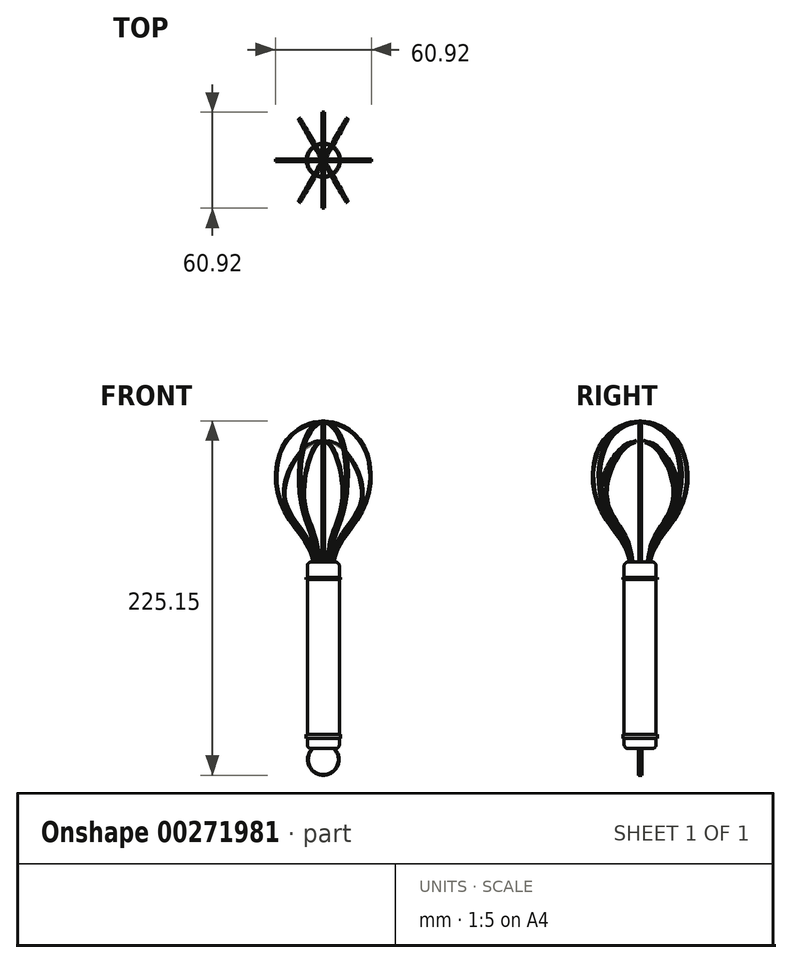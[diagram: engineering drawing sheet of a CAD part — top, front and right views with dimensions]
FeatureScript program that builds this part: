
annotation { "Feature Type Name" : "Feature", "Feature Type Description" : "" }
export const myFeature = defineFeature(function(context is Context, id is Id, definition is map)
    precondition{}
    {
        {
            var Q0;
            Q0=qCreatedBy(makeId("Front.planeOp"),FACE);
            var sketch = newSketch(context, id + "F0", { "sketchPlane" : qUnion([Q0])});
            skLineSegment(sketch, "E0", {"start": v(0, 93.33) * mm, "end": v(0, -97.58) * mm, "construction": true});
            skLineSegment(sketch, "E1.bottom", {"start": v(0, -73.35) * mm, "end": v(-7.62, -73.35) * mm});
            skLineSegment(sketch, "E1.top", {"start": v(0, 45.21) * mm, "end": v(-7.62, 45.21) * mm});
            skLineSegment(sketch, "E1.left", {"start": v(0, -73.35) * mm, "end": v(0, 45.21) * mm});
            skLineSegment(sketch, "E1.right", {"start": v(-10.16, -70.8) * mm, "end": v(-10.16, 42.67) * mm});
            skPoint(sketch, "E2.visualSharp", {"position": v(-10.16, -73.35) * mm});
            skArc(sketch, "E2.filletArc", {"start": v(-10.16, -70.8) * mm, "mid": v(-9.42, -72.6) * mm, "end": v(-7.62, -73.35) * mm});
            skPoint(sketch, "E3.visualSharp", {"position": v(-10.16, 45.21) * mm});
            skArc(sketch, "E3.filletArc", {"start": v(-7.62, 45.21) * mm, "mid": v(-9.42, 44.47) * mm, "end": v(-10.16, 42.67) * mm});
            skArc(sketch, "E4", {"start": v(-7.18, -73.35) * mm, "mid": v(0, -90.25) * mm, "end": v(7.18, -73.35) * mm});
            skPoint(sketch, "E5", {"position": v(-7.18, -73.35) * mm});
            skPoint(sketch, "E6", {"position": v(7.18, -73.35) * mm});
            skArc(sketch, "E7.0", {"start": v(-6.88, -73.63) * mm, "mid": v(0, -89.84) * mm, "end": v(6.88, -73.63) * mm});
            skFitSpline(sketch, "E8", {"points": [v(-6.88, -73.63) * mm, v(-6.6, -73.35) * mm], "startDerivative": vector(0.28, 0.28) * mm, "endDerivative": vector(0.28, 0.28) * mm});
            skLineSegment(sketch, "E9", {"start": v(-6.6, -73.35) * mm, "end": v(7.18, -73.35) * mm});
            skFitSpline(sketch, "E10", {"points": [v(6.88, -73.63) * mm, v(6.61, -73.35) * mm], "startDerivative": vector(-0.27, 0.28) * mm, "endDerivative": vector(-0.27, 0.28) * mm});
            skFitSpline(sketch, "E11", {"points": [v(-6.56, 45.21) * mm, v(-11.07, 60.4) * mm, v(-25.22, 86.5) * mm, v(-12.08, 117.9) * mm, v(0, 122.64) * mm], "startDerivative": vector(-9.97, 69.88) * mm, "endDerivative": vector(61.82, 8.5) * mm});
            skFitSpline(sketch, "E12.0", {"points": [v(-5.56, 45.35) * mm, v(-5.77, 46.81) * mm, v(-6.08, 49.02) * mm, v(-6.7, 52.03) * mm, v(-7.3, 54.33) * mm, v(-8.11, 56.67) * mm, v(-8.99, 58.67) * mm, v(-9.83, 60.3) * mm, v(-10.78, 61.93) * mm, v(-12.15, 64) * mm, v(-13.97, 66.51) * mm, v(-16.52, 69.96) * mm, v(-19.08, 73.57) * mm, v(-21.28, 77.37) * mm, v(-22.66, 80.33) * mm, v(-23.52, 82.89) * mm, v(-24, 85) * mm, v(-24.24, 86.62) * mm, v(-24.35, 88.29) * mm, v(-24.33, 90.56) * mm, v(-24.02, 93.48) * mm, v(-23.25, 97.04) * mm, v(-21.74, 101.76) * mm, v(-19.63, 106.3) * mm, v(-17.17, 110.37) * mm, v(-15.2, 113.12) * mm, v(-13.52, 115.1) * mm, v(-12.18, 116.45) * mm, v(-10.86, 117.64) * mm, v(-9.26, 118.81) * mm, v(-6.75, 120.17) * mm, v(-3.67, 121.1) * mm, v(-1.15, 121.46) * mm, v(0.14, 121.64) * mm]});
            skLineSegment(sketch, "E13", {"start": v(-5.56, 45.35) * mm, "end": v(-5.56, 45.21) * mm});
            skLineSegment(sketch, "E14", {"start": v(0.14, 121.64) * mm, "end": v(0, 122.64) * mm});
            skFitSpline(sketch, "E15.MirrorCS", {"points": [v(6.56, 45.21) * mm, v(11.07, 60.4) * mm, v(25.22, 86.5) * mm, v(12.08, 117.9) * mm, v(0, 122.64) * mm], "startDerivative": vector(9.97, 69.88) * mm, "endDerivative": vector(-61.82, 8.5) * mm});
            skFitSpline(sketch, "E16.0", {"points": [v(5.56, 45.35) * mm, v(5.77, 46.81) * mm, v(6.08, 49.02) * mm, v(6.7, 52.03) * mm, v(7.3, 54.33) * mm, v(8.11, 56.67) * mm, v(8.99, 58.67) * mm, v(9.83, 60.3) * mm, v(10.78, 61.93) * mm, v(12.15, 64) * mm, v(13.97, 66.51) * mm, v(16.52, 69.96) * mm, v(19.08, 73.57) * mm, v(21.28, 77.37) * mm, v(22.66, 80.33) * mm, v(23.52, 82.89) * mm, v(24, 85) * mm, v(24.24, 86.62) * mm, v(24.35, 88.29) * mm, v(24.33, 90.56) * mm, v(24.02, 93.48) * mm, v(23.25, 97.04) * mm, v(21.74, 101.76) * mm, v(19.63, 106.3) * mm, v(17.17, 110.37) * mm, v(15.2, 113.12) * mm, v(13.52, 115.1) * mm, v(12.18, 116.45) * mm, v(10.86, 117.64) * mm, v(9.26, 118.81) * mm, v(6.75, 120.17) * mm, v(3.67, 121.1) * mm, v(1.15, 121.46) * mm, v(-0.14, 121.64) * mm]});
            skLineSegment(sketch, "E17", {"start": v(0, 45.21) * mm, "end": v(6.56, 45.21) * mm});
            skLineSegment(sketch, "E18", {"start": v(5.56, 45.35) * mm, "end": v(5.56, 45.21) * mm});
            skLineSegment(sketch, "E19.bottom", {"start": v(-10.16, 34.07) * mm, "end": v(0, 34.07) * mm});
            skLineSegment(sketch, "E19.top", {"start": v(-10.16, 35.42) * mm, "end": v(0, 35.42) * mm});
            skLineSegment(sketch, "E19.left", {"start": v(-10.16, 34.07) * mm, "end": v(-10.16, 35.42) * mm});
            skLineSegment(sketch, "E19.right", {"start": v(0, 34.07) * mm, "end": v(0, 35.42) * mm});
            skLineSegment(sketch, "E20.bottom", {"start": v(0, -66.97) * mm, "end": v(-10.16, -66.97) * mm});
            skLineSegment(sketch, "E20.top", {"start": v(0, -64.16) * mm, "end": v(-10.16, -64.16) * mm});
            skLineSegment(sketch, "E20.left", {"start": v(0, -66.97) * mm, "end": v(0, -64.16) * mm});
            skLineSegment(sketch, "E20.right", {"start": v(-10.16, -66.97) * mm, "end": v(-10.16, -64.16) * mm});
            skLineSegment(sketch, "E21.bottom", {"start": v(-10.16, 35.42) * mm, "end": v(-10.84, 35.42) * mm});
            skLineSegment(sketch, "E21.top", {"start": v(-10.16, 34.07) * mm, "end": v(-10.84, 34.07) * mm});
            skLineSegment(sketch, "E21.left", {"start": v(-10.16, 35.42) * mm, "end": v(-10.16, 34.07) * mm});
            skLineSegment(sketch, "E21.right", {"start": v(-10.84, 35.42) * mm, "end": v(-10.84, 34.07) * mm});
            skLineSegment(sketch, "E22.bottom", {"start": v(-10.16, -66.97) * mm, "end": v(-10.84, -66.97) * mm});
            skLineSegment(sketch, "E22.top", {"start": v(-10.16, -64.16) * mm, "end": v(-10.84, -64.16) * mm});
            skLineSegment(sketch, "E22.right", {"start": v(-10.84, -66.97) * mm, "end": v(-10.84, -64.16) * mm});
            skSolve(sketch);
        }
        {
            var Q0;
            Q0=makeQuery(id+"F0.imprint","IMPRINT",FACE,{"disambiguationData":[TD([[makeQuery(id+"F0.imprint","IMPRINT",EDGE,{"derivedFrom":sQuery(id+"F0.wireOp",EDGE,"E1.top")}),1.0]])]});
            var Q1;
            Q1=sQuery(id+"F0.wireOp",EDGE,"E1.left");
            revolve(context, id + "F1", {"entities" : qUnion([Q0]), "axis" : qUnion([Q1]), "revolveType" : RevolveType.FULL});
        }
        {
            var Q0;
            {var subQ1=sQuery(id+"F0.wireOp",EDGE,"E4");Q0=makeQuery(id+"F0.imprint","IMPRINT",FACE,{"disambiguationData":[TD([[makeQuery(id+"F0.imprint","IMPRINT",EDGE,{"derivedFrom":subQ1}),1.0]])]});}
            extrude(context, id + "F2", {"entities" : qUnion([Q0]), "operationType" : NewBodyOperationType.ADD, "endBound" : BoundingType.SYMMETRIC, "depth" : 2.3 * mm});
        }
        {
            var Q0;
            Q0=makeQuery(id+"F2.opExtrude","CAP_EDGE",EDGE,{"disambiguationData":[OSD([sQuery(id+"F0.wireOp",EDGE,"E7.0")])],"isStart":false});
            fillet(context, id + "F3", {"entities" : qUnion([Q0]), "radius" : 0.43 * mm, "tangentPropagation" : true, "allowEdgeOverflow" : false});
        }
        {
            var Q0;
            Q0=makeQuery(id+"F2.opExtrude","CAP_EDGE",EDGE,{"disambiguationData":[OSD([sQuery(id+"F0.wireOp",EDGE,"E7.0")])],"isStart":true});
            fillet(context, id + "F4", {"entities" : qUnion([Q0]), "radius" : 0.67 * mm, "tangentPropagation" : true, "allowEdgeOverflow" : false});
        }
        {
            var Q0;
            Q0=makeQuery(id+"F3.opFillet","BLEND_EDGE",EDGE,{"blendedFrom":[makeQuery(id+"F2.opExtrude","CAP_EDGE",EDGE,{"disambiguationData":[OSD([sQuery(id+"F0.wireOp",EDGE,"E7.0")])],"isStart":false}),makeQuery(id+"F2.opExtrude","SWEPT_FACE",FACE,{"disambiguationData":[OSD([sQuery(id+"F0.wireOp",EDGE,"E4")])]})],"blendedInto":[makeQuery(id+"F2.opExtrude","SWEPT_FACE",FACE,{"disambiguationData":[OSD([sQuery(id+"F0.wireOp",EDGE,"E4")])]})]});
            fillet(context, id + "F5", {"entities" : qUnion([Q0]), "radius" : 0.17 * mm, "tangentPropagation" : true, "allowEdgeOverflow" : false});
        }
        {
            var Q0;
            {var subQ4=sQuery(id+"F0.wireOp",EDGE,"E11");Q0=makeQuery(id+"F0.imprint","IMPRINT",FACE,{"disambiguationData":[TD([[makeQuery(id+"F0.imprint","IMPRINT",EDGE,{"derivedFrom":subQ4}),-1.0]])]});}
            var Q1;
            {var subQ5=sQuery(id+"F0.wireOp",EDGE,"E14");Q1=makeQuery(id+"F0.imprint","IMPRINT",FACE,{"disambiguationData":[TD([[makeQuery(id+"F0.imprint","IMPRINT",EDGE,{"derivedFrom":subQ5}),-1.0]])]});}
            extrude(context, id + "F6", {"entities" : qUnion([Q0, Q1]), "endBound" : BoundingType.SYMMETRIC, "oppositeDirection" : true, "depth" : 0.5 * mm, "hasDraft" : true, "draftAngle" : 3 * degree});
        }
        {
            var Q0;
            Q0=qCreatedBy(makeId("Right.planeOp"),FACE);
            var sketch = newSketch(context, id + "F7", { "sketchPlane" : qUnion([Q0])});
            skFitSpline(sketch, "E23", {"points": [v(-6.67, 45.23) * mm, v(-10.44, 55.68) * mm, v(-27.99, 84.43) * mm, v(-25.65, 119.53) * mm, v(-10.27, 132.73) * mm, v(0, 134.9) * mm], "startDerivative": vector(-14.2, 65.3) * mm, "endDerivative": vector(68.76, 7.41) * mm});
            skFitSpline(sketch, "E24.MirrorCS", {"points": [v(6.67, 45.23) * mm, v(10.44, 55.68) * mm, v(27.99, 84.43) * mm, v(25.65, 119.53) * mm, v(10.27, 132.73) * mm, v(0, 134.9) * mm], "startDerivative": vector(14.2, 65.3) * mm, "endDerivative": vector(-68.76, 7.41) * mm});
            skFitSpline(sketch, "E25.0", {"points": [v(5.67, 45.45) * mm, v(5.82, 46.13) * mm, v(6.12, 47.5) * mm, v(6.68, 49.65) * mm, v(7.45, 51.93) * mm, v(8.35, 53.98) * mm, v(9.27, 55.71) * mm, v(10.35, 57.53) * mm, v(11.95, 59.92) * mm, v(14.17, 63) * mm, v(17.37, 67.38) * mm, v(20.71, 72.17) * mm, v(23.74, 77.3) * mm, v(25.41, 80.66) * mm, v(26.56, 83.42) * mm, v(27.56, 86.23) * mm, v(28.52, 89.84) * mm, v(29.23, 94.26) * mm, v(29.5, 98.7) * mm, v(29.38, 103.08) * mm, v(28.85, 107.34) * mm, v(27.94, 111.4) * mm, v(26.67, 115.2) * mm, v(25.07, 118.65) * mm, v(23.14, 121.69) * mm, v(20.94, 124.35) * mm, v(18.55, 126.63) * mm, v(16.04, 128.56) * mm, v(13.5, 130.14) * mm, v(11.4, 131.17) * mm, v(9.79, 131.84) * mm, v(8.22, 132.4) * mm, v(6.34, 132.93) * mm, v(3.44, 133.5) * mm, v(1.32, 133.74) * mm, v(-0.1, 133.9) * mm]});
            skFitSpline(sketch, "E25.1", {"points": [v(-5.67, 45.45) * mm, v(-5.82, 46.13) * mm, v(-6.12, 47.5) * mm, v(-6.68, 49.65) * mm, v(-7.45, 51.93) * mm, v(-8.35, 53.98) * mm, v(-9.27, 55.71) * mm, v(-10.35, 57.53) * mm, v(-11.95, 59.92) * mm, v(-14.17, 63) * mm, v(-17.37, 67.38) * mm, v(-20.71, 72.17) * mm, v(-23.74, 77.3) * mm, v(-25.41, 80.66) * mm, v(-26.56, 83.42) * mm, v(-27.56, 86.23) * mm, v(-28.52, 89.84) * mm, v(-29.23, 94.26) * mm, v(-29.5, 98.7) * mm, v(-29.38, 103.08) * mm, v(-28.85, 107.34) * mm, v(-27.94, 111.4) * mm, v(-26.67, 115.2) * mm, v(-25.07, 118.65) * mm, v(-23.14, 121.69) * mm, v(-20.94, 124.35) * mm, v(-18.55, 126.63) * mm, v(-16.04, 128.56) * mm, v(-13.5, 130.14) * mm, v(-11.4, 131.17) * mm, v(-9.79, 131.84) * mm, v(-8.22, 132.4) * mm, v(-6.34, 132.93) * mm, v(-3.44, 133.5) * mm, v(-1.32, 133.74) * mm, v(0.1, 133.9) * mm]});
            skLineSegment(sketch, "E26", {"start": v(-6.67, 45.23) * mm, "end": v(6.67, 45.23) * mm});
            skLineSegment(sketch, "E27", {"start": v(5.67, 45.45) * mm, "end": v(5.67, 45.23) * mm});
            skLineSegment(sketch, "E28", {"start": v(-5.67, 45.45) * mm, "end": v(-5.67, 45.23) * mm});
            skSolve(sketch);
        }
        {
            var Q0;
            {var subQ1=sQuery(id+"F7.wireOp",EDGE,"E23");Q0=makeQuery(id+"F7.imprint","IMPRINT",FACE,{"disambiguationData":[TD([[makeQuery(id+"F7.imprint","IMPRINT",EDGE,{"derivedFrom":subQ1}),-1.0]])]});}
            extrude(context, id + "F8", {"entities" : qUnion([Q0]), "endBound" : BoundingType.SYMMETRIC, "oppositeDirection" : true, "depth" : 1.52 * mm});
        }
        {
            var Q0;
            Q0=makeQuery(id+"F8.opExtrude","SWEPT_BODY",BODY,{"disambiguationData":[OSD([sQuery(id+"F7.wireOp",EDGE,"E23"),sQuery(id+"F7.wireOp",EDGE,"E24.MirrorCS"),sQuery(id+"F7.wireOp",EDGE,"E25.0"),sQuery(id+"F7.wireOp",EDGE,"E25.1"),sQuery(id+"F7.wireOp",EDGE,"E26"),sQuery(id+"F7.wireOp",EDGE,"E27"),sQuery(id+"F7.wireOp",EDGE,"E28")])]});
            var Q1;
            Q1=makeQuery(id+"F6.*.split.splitOp","SPLIT",BODY,{"derivedFrom":makeQuery(id+"F6.opExtrude","SWEPT_BODY",BODY,{"disambiguationData":[OSD([sQuery(id+"F0.wireOp",EDGE,"E1.top"),sQuery(id+"F0.wireOp",EDGE,"E11"),sQuery(id+"F0.wireOp",EDGE,"E12.0"),sQuery(id+"F0.wireOp",EDGE,"E13"),sQuery(id+"F0.wireOp",EDGE,"E15.MirrorCS"),sQuery(id+"F0.wireOp",EDGE,"E16.0"),sQuery(id+"F0.wireOp",EDGE,"E17"),sQuery(id+"F0.wireOp",EDGE,"E18")])]})});
            var Q2;
            Q2=sQuery(id+"F0.wireOp",EDGE,"E0");
            circularPattern(context, id + "F9", {"entities" : qUnion([Q0, Q1]), "axis" : qUnion([Q2]), "angle" : 360 * degree, "instanceCount" : 4, "oppositeDirection" : true, "equalSpace" : true});
        }
        {
            var Q0;
            Q0=makeQuery(id+"F9.opPattern","COPY",BODY,{"derivedFrom":makeQuery(id+"F8.opExtrude","SWEPT_BODY",BODY,{"disambiguationData":[OSD([sQuery(id+"F7.wireOp",EDGE,"E23"),sQuery(id+"F7.wireOp",EDGE,"E24.MirrorCS"),sQuery(id+"F7.wireOp",EDGE,"E25.0"),sQuery(id+"F7.wireOp",EDGE,"E25.1"),sQuery(id+"F7.wireOp",EDGE,"E26"),sQuery(id+"F7.wireOp",EDGE,"E27"),sQuery(id+"F7.wireOp",EDGE,"E28")])]}),"instanceName":"1"});
            var Q1;
            Q1=makeQuery(id+"F6.*.split.splitOp","SPLIT",BODY,{"derivedFrom":makeQuery(id+"F6.opExtrude","SWEPT_BODY",BODY,{"disambiguationData":[OSD([sQuery(id+"F0.wireOp",EDGE,"E1.top"),sQuery(id+"F0.wireOp",EDGE,"E11"),sQuery(id+"F0.wireOp",EDGE,"E12.0"),sQuery(id+"F0.wireOp",EDGE,"E13"),sQuery(id+"F0.wireOp",EDGE,"E15.MirrorCS"),sQuery(id+"F0.wireOp",EDGE,"E16.0"),sQuery(id+"F0.wireOp",EDGE,"E17"),sQuery(id+"F0.wireOp",EDGE,"E18")])]})});
            var Q2;
            Q2=sQuery(id+"F0.wireOp",EDGE,"E0");
            circularPattern(context, id + "F10", {"entities" : qUnion([Q0, Q1]), "axis" : qUnion([Q2]), "angle" : 180 * degree, "instanceCount" : 4, "equalSpace" : true});
        }
        {
            var Q0;
            {var subQ0=sQuery(id+"F0.wireOp",EDGE,"E19.bottom");Q0=makeQuery(id+"F0.imprint","IMPRINT",FACE,{"disambiguationData":[TD([[makeQuery(id+"F0.imprint","IMPRINT",EDGE,{"derivedFrom":subQ0}),-1.0]])]});}
            var Q1;
            {var subQ0=sQuery(id+"F0.wireOp",EDGE,"E2.filletArc");Q1=makeQuery(id+"F0.imprint","IMPRINT",FACE,{"disambiguationData":[TD([[makeQuery(id+"F0.imprint","IMPRINT",EDGE,{"derivedFrom":subQ0}),1.0]])]});}
            var Q2;
            Q2=sQuery(id+"F0.wireOp",EDGE,"E1.left");
            revolve(context, id + "F11", {"entities" : qUnion([Q0, Q1]), "axis" : qUnion([Q2]), "revolveType" : RevolveType.FULL});
        }
        {
            var Q0;
            Q0=makeQuery(id+"F0.imprint","IMPRINT",FACE,{"disambiguationData":[TD([[makeQuery(id+"F0.imprint","IMPRINT",EDGE,{"derivedFrom":sQuery(id+"F0.wireOp",EDGE,"E20.bottom")}),-1.0]])]});
            var Q1;
            Q1=makeQuery(id+"F0.imprint","IMPRINT",FACE,{"disambiguationData":[TD([[makeQuery(id+"F0.imprint","IMPRINT",EDGE,{"derivedFrom":sQuery(id+"F0.wireOp",EDGE,"E22.bottom")}),-1.0]])]});
            var Q2;
            Q2=makeQuery(id+"F0.imprint","IMPRINT",FACE,{"disambiguationData":[TD([[makeQuery(id+"F0.imprint","IMPRINT",EDGE,{"derivedFrom":sQuery(id+"F0.wireOp",EDGE,"E21.bottom")}),1.0]])]});
            var Q3;
            Q3=makeQuery(id+"F0.imprint","IMPRINT",FACE,{"disambiguationData":[TD([[makeQuery(id+"F0.imprint","IMPRINT",EDGE,{"derivedFrom":sQuery(id+"F0.wireOp",EDGE,"E19.bottom")}),1.0]])]});
            var Q4;
            Q4=sQuery(id+"F0.wireOp",EDGE,"E1.left");
            revolve(context, id + "F12", {"entities" : qUnion([Q0, Q1, Q2, Q3]), "axis" : qUnion([Q4]), "revolveType" : RevolveType.FULL});
        }
    });
